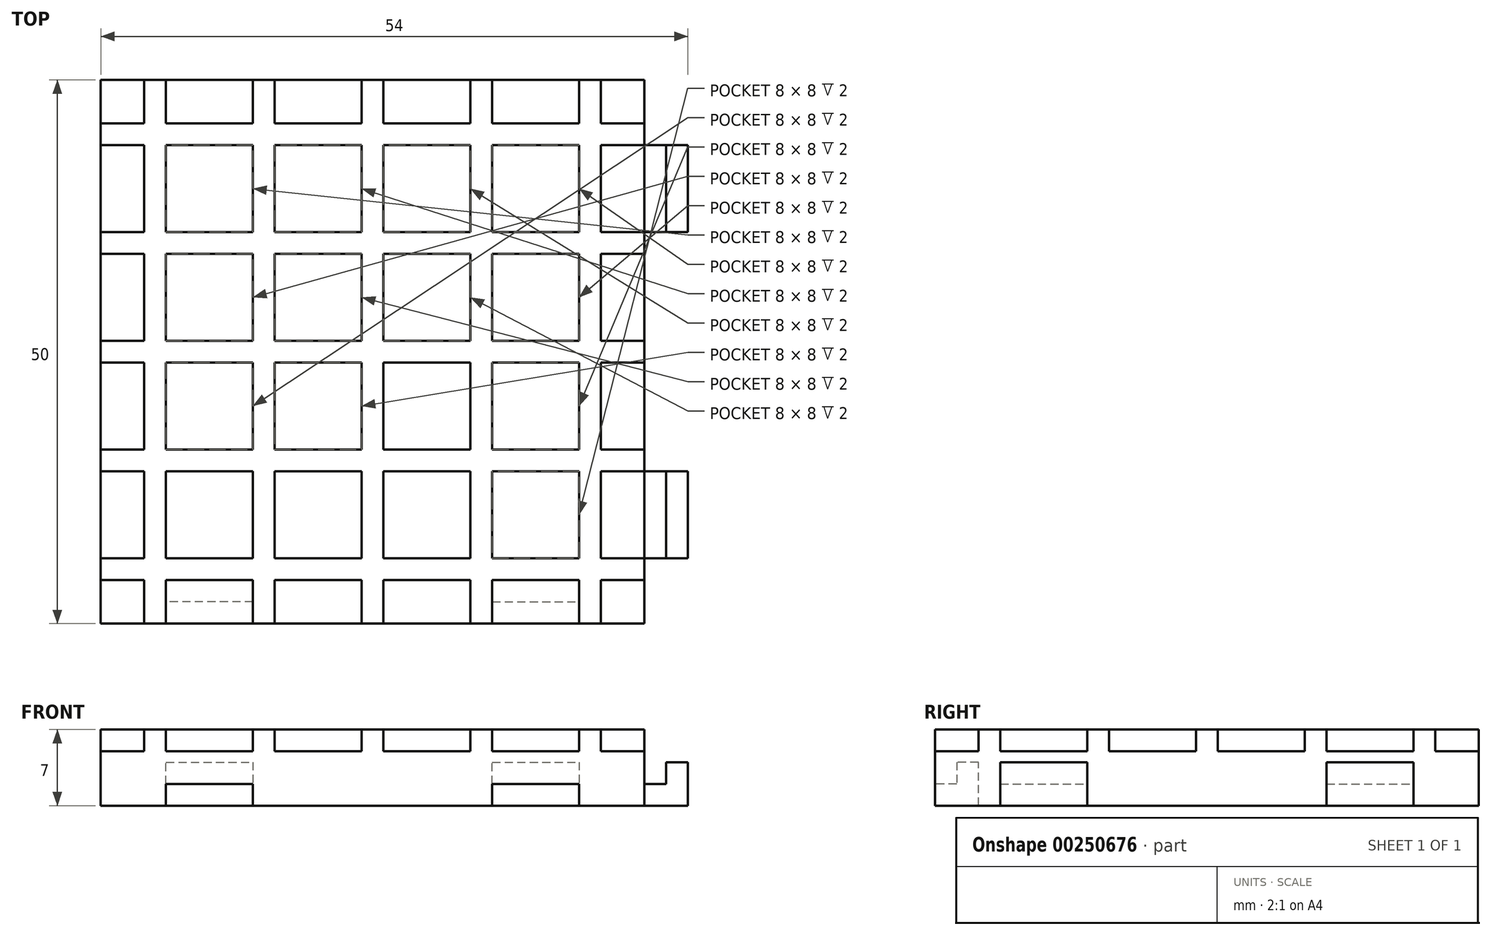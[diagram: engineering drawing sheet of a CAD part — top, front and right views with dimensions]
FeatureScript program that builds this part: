
annotation { "Feature Type Name" : "Feature", "Feature Type Description" : "" }
export const myFeature = defineFeature(function(context is Context, id is Id, definition is map)
    precondition{}
    {
        {
            var Q0;
            Q0=qCreatedBy(makeId("Top.planeOp"),FACE);
            var sketch = newSketch(context, id + "F0", { "sketchPlane" : qUnion([Q0])});
            skLineSegment(sketch, "E0.bottom", {"start": v(-29.37, 40.47) * mm, "end": v(20.63, 40.47) * mm});
            skLineSegment(sketch, "E0.top", {"start": v(-29.37, -9.53) * mm, "end": v(20.63, -9.53) * mm});
            skLineSegment(sketch, "E0.left", {"start": v(-29.37, 40.47) * mm, "end": v(-29.37, -9.53) * mm});
            skLineSegment(sketch, "E0.right", {"start": v(20.63, 40.47) * mm, "end": v(20.63, -9.53) * mm});
            skSolve(sketch);
        }
        {
            var Q0;
            Q0=qSketchRegion(id+"F0",true);
            extrude(context, id + "F1", {"entities" : qUnion([Q0]), "depth" : 5 * mm});
        }
        {
            var Q0;
            Q0=makeQuery(id+"F1.opExtrude","CAP_FACE",FACE,{"disambiguationData":[OSD([sQuery(id+"F0.wireOp",EDGE,"E0.bottom"),sQuery(id+"F0.wireOp",EDGE,"E0.top"),sQuery(id+"F0.wireOp",EDGE,"E0.left"),sQuery(id+"F0.wireOp",EDGE,"E0.right")])],"isStart":false});
            var sketch = newSketch(context, id + "F2", { "sketchPlane" : qUnion([Q0])});
            skLineSegment(sketch, "E1.bottom", {"start": v(-29.37, -5.53) * mm, "end": v(20.63, -5.53) * mm});
            skLineSegment(sketch, "E1.top", {"start": v(-29.37, -3.53) * mm, "end": v(20.63, -3.53) * mm});
            skLineSegment(sketch, "E1.left", {"start": v(-29.37, -5.53) * mm, "end": v(-29.37, -3.53) * mm});
            skLineSegment(sketch, "E1.right", {"start": v(20.63, -5.53) * mm, "end": v(20.63, -3.53) * mm});
            skLineSegment(sketch, "E2.bottom", {"start": v(-29.37, 4.47) * mm, "end": v(20.63, 4.47) * mm});
            skLineSegment(sketch, "E2.top", {"start": v(-29.37, 6.47) * mm, "end": v(20.63, 6.47) * mm});
            skLineSegment(sketch, "E2.left", {"start": v(-29.37, 4.47) * mm, "end": v(-29.37, 6.47) * mm});
            skLineSegment(sketch, "E2.right", {"start": v(20.63, 4.47) * mm, "end": v(20.63, 6.47) * mm});
            skLineSegment(sketch, "E3.bottom", {"start": v(-29.37, 14.47) * mm, "end": v(20.63, 14.47) * mm});
            skLineSegment(sketch, "E3.top", {"start": v(-29.37, 16.47) * mm, "end": v(20.63, 16.47) * mm});
            skLineSegment(sketch, "E3.left", {"start": v(-29.37, 14.47) * mm, "end": v(-29.37, 16.47) * mm});
            skLineSegment(sketch, "E3.right", {"start": v(20.63, 14.47) * mm, "end": v(20.63, 16.47) * mm});
            skLineSegment(sketch, "E4.bottom", {"start": v(-29.37, 24.47) * mm, "end": v(20.63, 24.47) * mm});
            skLineSegment(sketch, "E4.top", {"start": v(-29.37, 26.47) * mm, "end": v(20.63, 26.47) * mm});
            skLineSegment(sketch, "E4.left", {"start": v(-29.37, 24.47) * mm, "end": v(-29.37, 26.47) * mm});
            skLineSegment(sketch, "E4.right", {"start": v(20.63, 24.47) * mm, "end": v(20.63, 26.47) * mm});
            skLineSegment(sketch, "E5.bottom", {"start": v(-29.37, 34.47) * mm, "end": v(20.63, 34.47) * mm});
            skLineSegment(sketch, "E5.top", {"start": v(-29.37, 36.47) * mm, "end": v(20.63, 36.47) * mm});
            skLineSegment(sketch, "E5.left", {"start": v(-29.37, 34.47) * mm, "end": v(-29.37, 36.47) * mm});
            skLineSegment(sketch, "E5.right", {"start": v(20.63, 34.47) * mm, "end": v(20.63, 36.47) * mm});
            skLineSegment(sketch, "E6.bottom", {"start": v(-25.37, -9.53) * mm, "end": v(-23.37, -9.53) * mm});
            skLineSegment(sketch, "E6.top", {"start": v(-25.37, 40.47) * mm, "end": v(-23.37, 40.47) * mm});
            skLineSegment(sketch, "E6.left", {"start": v(-25.37, -9.53) * mm, "end": v(-25.37, 40.47) * mm});
            skLineSegment(sketch, "E6.right", {"start": v(-23.37, -9.53) * mm, "end": v(-23.37, 40.47) * mm});
            skLineSegment(sketch, "E7.bottom", {"start": v(-15.37, -9.53) * mm, "end": v(-13.37, -9.53) * mm});
            skLineSegment(sketch, "E7.top", {"start": v(-15.37, 40.47) * mm, "end": v(-13.37, 40.47) * mm});
            skLineSegment(sketch, "E7.left", {"start": v(-15.37, -9.53) * mm, "end": v(-15.37, 40.47) * mm});
            skLineSegment(sketch, "E7.right", {"start": v(-13.37, -9.53) * mm, "end": v(-13.37, 40.47) * mm});
            skLineSegment(sketch, "E8.bottom", {"start": v(-5.37, -9.53) * mm, "end": v(-3.37, -9.53) * mm});
            skLineSegment(sketch, "E8.top", {"start": v(-5.37, 40.47) * mm, "end": v(-3.37, 40.47) * mm});
            skLineSegment(sketch, "E8.left", {"start": v(-5.37, -9.53) * mm, "end": v(-5.37, 40.47) * mm});
            skLineSegment(sketch, "E8.right", {"start": v(-3.37, -9.53) * mm, "end": v(-3.37, 40.47) * mm});
            skLineSegment(sketch, "E9.bottom", {"start": v(4.63, -9.53) * mm, "end": v(6.63, -9.53) * mm});
            skLineSegment(sketch, "E9.top", {"start": v(4.63, 40.47) * mm, "end": v(6.63, 40.47) * mm});
            skLineSegment(sketch, "E9.left", {"start": v(4.63, -9.53) * mm, "end": v(4.63, 40.47) * mm});
            skLineSegment(sketch, "E9.right", {"start": v(6.63, -9.53) * mm, "end": v(6.63, 40.47) * mm});
            skLineSegment(sketch, "E10.bottom", {"start": v(14.63, -9.53) * mm, "end": v(16.63, -9.53) * mm});
            skLineSegment(sketch, "E10.top", {"start": v(14.63, 40.47) * mm, "end": v(16.63, 40.47) * mm});
            skLineSegment(sketch, "E10.left", {"start": v(14.63, -9.53) * mm, "end": v(14.63, 40.47) * mm});
            skLineSegment(sketch, "E10.right", {"start": v(16.63, -9.53) * mm, "end": v(16.63, 40.47) * mm});
            skSolve(sketch);
        }
        {
            var Q0;
            Q0=makeQuery(id+"F4.boolean.opBoolean","MERGE",FACE,{"derivedFrom":[makeQuery(id+"F1.opExtrude","SWEPT_FACE",FACE,{"disambiguationData":[OSD([sQuery(id+"F0.wireOp",EDGE,"E0.top")])]}),makeQuery(id+"F4.opExtrude","SWEPT_FACE",FACE,{"disambiguationData":[OSD([sQuery(id+"F2.wireOp",EDGE,"E6.bottom")])]}),makeQuery(id+"F4.opExtrude","SWEPT_FACE",FACE,{"disambiguationData":[OSD([sQuery(id+"F2.wireOp",EDGE,"E7.bottom")])]}),makeQuery(id+"F4.opExtrude","SWEPT_FACE",FACE,{"disambiguationData":[OSD([sQuery(id+"F2.wireOp",EDGE,"E8.bottom")])]}),makeQuery(id+"F4.opExtrude","SWEPT_FACE",FACE,{"disambiguationData":[OSD([sQuery(id+"F2.wireOp",EDGE,"E9.bottom")])]}),makeQuery(id+"F4.opExtrude","SWEPT_FACE",FACE,{"disambiguationData":[OSD([sQuery(id+"F2.wireOp",EDGE,"E10.bottom")])]})]});
            var sketch = newSketch(context, id + "F3", { "sketchPlane" : qUnion([Q0])});
            skLineSegment(sketch, "E11.bottom", {"start": v(-23.37, 0) * mm, "end": v(-15.37, 0) * mm});
            skLineSegment(sketch, "E11.top", {"start": v(-23.37, 2) * mm, "end": v(-15.37, 2) * mm});
            skLineSegment(sketch, "E11.left", {"start": v(-23.37, 0) * mm, "end": v(-23.37, 2) * mm});
            skLineSegment(sketch, "E11.right", {"start": v(-15.37, 0) * mm, "end": v(-15.37, 2) * mm});
            skLineSegment(sketch, "E12.bottom", {"start": v(6.63, 0) * mm, "end": v(14.63, 0) * mm});
            skLineSegment(sketch, "E12.top", {"start": v(6.63, 2) * mm, "end": v(14.63, 2) * mm});
            skLineSegment(sketch, "E12.left", {"start": v(6.63, 0) * mm, "end": v(6.63, 2) * mm});
            skLineSegment(sketch, "E12.right", {"start": v(14.63, 0) * mm, "end": v(14.63, 2) * mm});
            skSolve(sketch);
        }
        {
            var Q0;
            Q0=qSketchRegion(id+"F2",true);
            var Q1;
            {var subQ0=sQuery(id+"F2.wireOp",EDGE,"E7.left");var subQ1=sQuery(id+"F2.wireOp",EDGE,"E1.top");var subQ2=makeQuery(id+"F2.imprint","INTERSECT",VERTEX,{"derivedFrom":[subQ1,subQ0]});Q1=makeQuery(id+"F2.imprint","IMPRINT",FACE,{"disambiguationData":[TD([[makeQuery(id+"F2.imprint","IMPRINT",EDGE,{"disambiguationData":[TD([[subQ2,-1.0]])],"derivedFrom":subQ1}),1.0]])]});}
            var Q2;
            {var subQ0=sQuery(id+"F2.wireOp",EDGE,"E7.left");var subQ1=sQuery(id+"F2.wireOp",EDGE,"E2.bottom");var subQ2=makeQuery(id+"F2.imprint","INTERSECT",VERTEX,{"derivedFrom":[subQ1,subQ0]});Q2=makeQuery(id+"F2.imprint","IMPRINT",FACE,{"disambiguationData":[TD([[makeQuery(id+"F2.imprint","IMPRINT",EDGE,{"disambiguationData":[TD([[subQ2,-1.0]])],"derivedFrom":subQ1}),1.0]])]});}
            var Q3;
            {var subQ0=sQuery(id+"F2.wireOp",EDGE,"E7.right");var subQ1=sQuery(id+"F2.wireOp",EDGE,"E2.bottom");var subQ2=makeQuery(id+"F2.imprint","INTERSECT",VERTEX,{"derivedFrom":[subQ1,subQ0]});Q3=makeQuery(id+"F2.imprint","IMPRINT",FACE,{"disambiguationData":[TD([[makeQuery(id+"F2.imprint","IMPRINT",EDGE,{"disambiguationData":[TD([[subQ2,-1.0]])],"derivedFrom":subQ1}),1.0]])]});}
            var Q4;
            {var subQ0=sQuery(id+"F2.wireOp",EDGE,"E7.left");var subQ1=sQuery(id+"F2.wireOp",EDGE,"E2.top");var subQ2=makeQuery(id+"F2.imprint","INTERSECT",VERTEX,{"derivedFrom":[subQ1,subQ0]});Q4=makeQuery(id+"F2.imprint","IMPRINT",FACE,{"disambiguationData":[TD([[makeQuery(id+"F2.imprint","IMPRINT",EDGE,{"disambiguationData":[TD([[subQ2,-1.0]])],"derivedFrom":subQ1}),1.0]])]});}
            var Q5;
            {var subQ0=sQuery(id+"F2.wireOp",EDGE,"E7.left");var subQ1=sQuery(id+"F2.wireOp",EDGE,"E3.bottom");var subQ2=makeQuery(id+"F2.imprint","INTERSECT",VERTEX,{"derivedFrom":[subQ1,subQ0]});Q5=makeQuery(id+"F2.imprint","IMPRINT",FACE,{"disambiguationData":[TD([[makeQuery(id+"F2.imprint","IMPRINT",EDGE,{"disambiguationData":[TD([[subQ2,-1.0]])],"derivedFrom":subQ1}),1.0]])]});}
            var Q6;
            {var subQ0=sQuery(id+"F2.wireOp",EDGE,"E6.right");var subQ1=sQuery(id+"F2.wireOp",EDGE,"E3.bottom");var subQ2=makeQuery(id+"F2.imprint","INTERSECT",VERTEX,{"derivedFrom":[subQ1,subQ0]});Q6=makeQuery(id+"F2.imprint","IMPRINT",FACE,{"disambiguationData":[TD([[makeQuery(id+"F2.imprint","IMPRINT",EDGE,{"disambiguationData":[TD([[subQ2,-1.0]])],"derivedFrom":subQ1}),1.0]])]});}
            var Q7;
            {var subQ0=sQuery(id+"F2.wireOp",EDGE,"E6.right");var subQ1=sQuery(id+"F2.wireOp",EDGE,"E4.bottom");var subQ2=makeQuery(id+"F2.imprint","INTERSECT",VERTEX,{"derivedFrom":[subQ1,subQ0]});Q7=makeQuery(id+"F2.imprint","IMPRINT",FACE,{"disambiguationData":[TD([[makeQuery(id+"F2.imprint","IMPRINT",EDGE,{"disambiguationData":[TD([[subQ2,-1.0]])],"derivedFrom":subQ1}),1.0]])]});}
            var Q8;
            {var subQ0=sQuery(id+"F2.wireOp",EDGE,"E7.left");var subQ1=sQuery(id+"F2.wireOp",EDGE,"E4.bottom");var subQ2=makeQuery(id+"F2.imprint","INTERSECT",VERTEX,{"derivedFrom":[subQ1,subQ0]});Q8=makeQuery(id+"F2.imprint","IMPRINT",FACE,{"disambiguationData":[TD([[makeQuery(id+"F2.imprint","IMPRINT",EDGE,{"disambiguationData":[TD([[subQ2,-1.0]])],"derivedFrom":subQ1}),1.0]])]});}
            var Q9;
            {var subQ0=sQuery(id+"F2.wireOp",EDGE,"E7.left");var subQ1=sQuery(id+"F2.wireOp",EDGE,"E4.top");var subQ2=makeQuery(id+"F2.imprint","INTERSECT",VERTEX,{"derivedFrom":[subQ1,subQ0]});Q9=makeQuery(id+"F2.imprint","IMPRINT",FACE,{"disambiguationData":[TD([[makeQuery(id+"F2.imprint","IMPRINT",EDGE,{"disambiguationData":[TD([[subQ2,-1.0]])],"derivedFrom":subQ1}),1.0]])]});}
            var Q10;
            {var subQ0=sQuery(id+"F2.wireOp",EDGE,"E7.left");var subQ1=sQuery(id+"F2.wireOp",EDGE,"E3.top");var subQ2=makeQuery(id+"F2.imprint","INTERSECT",VERTEX,{"derivedFrom":[subQ1,subQ0]});Q10=makeQuery(id+"F2.imprint","IMPRINT",FACE,{"disambiguationData":[TD([[makeQuery(id+"F2.imprint","IMPRINT",EDGE,{"disambiguationData":[TD([[subQ2,-1.0]])],"derivedFrom":subQ1}),1.0]])]});}
            var Q11;
            {var subQ0=sQuery(id+"F2.wireOp",EDGE,"E7.right");var subQ1=sQuery(id+"F2.wireOp",EDGE,"E4.bottom");var subQ2=makeQuery(id+"F2.imprint","INTERSECT",VERTEX,{"derivedFrom":[subQ1,subQ0]});Q11=makeQuery(id+"F2.imprint","IMPRINT",FACE,{"disambiguationData":[TD([[makeQuery(id+"F2.imprint","IMPRINT",EDGE,{"disambiguationData":[TD([[subQ2,-1.0]])],"derivedFrom":subQ1}),1.0]])]});}
            var Q12;
            {var subQ0=sQuery(id+"F2.wireOp",EDGE,"E8.left");var subQ1=sQuery(id+"F2.wireOp",EDGE,"E3.top");var subQ2=makeQuery(id+"F2.imprint","INTERSECT",VERTEX,{"derivedFrom":[subQ1,subQ0]});Q12=makeQuery(id+"F2.imprint","IMPRINT",FACE,{"disambiguationData":[TD([[makeQuery(id+"F2.imprint","IMPRINT",EDGE,{"disambiguationData":[TD([[subQ2,-1.0]])],"derivedFrom":subQ1}),1.0]])]});}
            var Q13;
            {var subQ0=sQuery(id+"F2.wireOp",EDGE,"E8.left");var subQ1=sQuery(id+"F2.wireOp",EDGE,"E3.bottom");var subQ2=makeQuery(id+"F2.imprint","INTERSECT",VERTEX,{"derivedFrom":[subQ1,subQ0]});Q13=makeQuery(id+"F2.imprint","IMPRINT",FACE,{"disambiguationData":[TD([[makeQuery(id+"F2.imprint","IMPRINT",EDGE,{"disambiguationData":[TD([[subQ2,-1.0]])],"derivedFrom":subQ1}),1.0]])]});}
            var Q14;
            {var subQ0=sQuery(id+"F2.wireOp",EDGE,"E7.right");var subQ1=sQuery(id+"F2.wireOp",EDGE,"E3.bottom");var subQ2=makeQuery(id+"F2.imprint","INTERSECT",VERTEX,{"derivedFrom":[subQ1,subQ0]});Q14=makeQuery(id+"F2.imprint","IMPRINT",FACE,{"disambiguationData":[TD([[makeQuery(id+"F2.imprint","IMPRINT",EDGE,{"disambiguationData":[TD([[subQ2,-1.0]])],"derivedFrom":subQ1}),1.0]])]});}
            var Q15;
            {var subQ0=sQuery(id+"F2.wireOp",EDGE,"E8.left");var subQ1=sQuery(id+"F2.wireOp",EDGE,"E2.top");var subQ2=makeQuery(id+"F2.imprint","INTERSECT",VERTEX,{"derivedFrom":[subQ1,subQ0]});Q15=makeQuery(id+"F2.imprint","IMPRINT",FACE,{"disambiguationData":[TD([[makeQuery(id+"F2.imprint","IMPRINT",EDGE,{"disambiguationData":[TD([[subQ2,-1.0]])],"derivedFrom":subQ1}),1.0]])]});}
            var Q16;
            {var subQ0=sQuery(id+"F2.wireOp",EDGE,"E8.left");var subQ1=sQuery(id+"F2.wireOp",EDGE,"E2.bottom");var subQ2=makeQuery(id+"F2.imprint","INTERSECT",VERTEX,{"derivedFrom":[subQ1,subQ0]});Q16=makeQuery(id+"F2.imprint","IMPRINT",FACE,{"disambiguationData":[TD([[makeQuery(id+"F2.imprint","IMPRINT",EDGE,{"disambiguationData":[TD([[subQ2,-1.0]])],"derivedFrom":subQ1}),1.0]])]});}
            var Q17;
            {var subQ0=sQuery(id+"F2.wireOp",EDGE,"E8.left");var subQ1=sQuery(id+"F2.wireOp",EDGE,"E1.top");var subQ2=makeQuery(id+"F2.imprint","INTERSECT",VERTEX,{"derivedFrom":[subQ1,subQ0]});Q17=makeQuery(id+"F2.imprint","IMPRINT",FACE,{"disambiguationData":[TD([[makeQuery(id+"F2.imprint","IMPRINT",EDGE,{"disambiguationData":[TD([[subQ2,-1.0]])],"derivedFrom":subQ1}),1.0]])]});}
            var Q18;
            {var subQ0=sQuery(id+"F2.wireOp",EDGE,"E8.right");var subQ1=sQuery(id+"F2.wireOp",EDGE,"E2.bottom");var subQ2=makeQuery(id+"F2.imprint","INTERSECT",VERTEX,{"derivedFrom":[subQ1,subQ0]});Q18=makeQuery(id+"F2.imprint","IMPRINT",FACE,{"disambiguationData":[TD([[makeQuery(id+"F2.imprint","IMPRINT",EDGE,{"disambiguationData":[TD([[subQ2,-1.0]])],"derivedFrom":subQ1}),1.0]])]});}
            var Q19;
            {var subQ0=sQuery(id+"F2.wireOp",EDGE,"E9.left");var subQ1=sQuery(id+"F2.wireOp",EDGE,"E1.top");var subQ2=makeQuery(id+"F2.imprint","INTERSECT",VERTEX,{"derivedFrom":[subQ1,subQ0]});Q19=makeQuery(id+"F2.imprint","IMPRINT",FACE,{"disambiguationData":[TD([[makeQuery(id+"F2.imprint","IMPRINT",EDGE,{"disambiguationData":[TD([[subQ2,-1.0]])],"derivedFrom":subQ1}),1.0]])]});}
            var Q20;
            {var subQ0=sQuery(id+"F2.wireOp",EDGE,"E9.left");var subQ1=sQuery(id+"F2.wireOp",EDGE,"E2.bottom");var subQ2=makeQuery(id+"F2.imprint","INTERSECT",VERTEX,{"derivedFrom":[subQ1,subQ0]});Q20=makeQuery(id+"F2.imprint","IMPRINT",FACE,{"disambiguationData":[TD([[makeQuery(id+"F2.imprint","IMPRINT",EDGE,{"disambiguationData":[TD([[subQ2,-1.0]])],"derivedFrom":subQ1}),1.0]])]});}
            var Q21;
            {var subQ0=sQuery(id+"F2.wireOp",EDGE,"E9.right");var subQ1=sQuery(id+"F2.wireOp",EDGE,"E2.bottom");var subQ2=makeQuery(id+"F2.imprint","INTERSECT",VERTEX,{"derivedFrom":[subQ1,subQ0]});Q21=makeQuery(id+"F2.imprint","IMPRINT",FACE,{"disambiguationData":[TD([[makeQuery(id+"F2.imprint","IMPRINT",EDGE,{"disambiguationData":[TD([[subQ2,-1.0]])],"derivedFrom":subQ1}),1.0]])]});}
            var Q22;
            {var subQ0=sQuery(id+"F2.wireOp",EDGE,"E9.left");var subQ1=sQuery(id+"F2.wireOp",EDGE,"E2.top");var subQ2=makeQuery(id+"F2.imprint","INTERSECT",VERTEX,{"derivedFrom":[subQ1,subQ0]});Q22=makeQuery(id+"F2.imprint","IMPRINT",FACE,{"disambiguationData":[TD([[makeQuery(id+"F2.imprint","IMPRINT",EDGE,{"disambiguationData":[TD([[subQ2,-1.0]])],"derivedFrom":subQ1}),1.0]])]});}
            var Q23;
            {var subQ0=sQuery(id+"F2.wireOp",EDGE,"E9.right");var subQ1=sQuery(id+"F2.wireOp",EDGE,"E3.bottom");var subQ2=makeQuery(id+"F2.imprint","INTERSECT",VERTEX,{"derivedFrom":[subQ1,subQ0]});Q23=makeQuery(id+"F2.imprint","IMPRINT",FACE,{"disambiguationData":[TD([[makeQuery(id+"F2.imprint","IMPRINT",EDGE,{"disambiguationData":[TD([[subQ2,-1.0]])],"derivedFrom":subQ1}),1.0]])]});}
            var Q24;
            {var subQ0=sQuery(id+"F2.wireOp",EDGE,"E9.left");var subQ1=sQuery(id+"F2.wireOp",EDGE,"E3.bottom");var subQ2=makeQuery(id+"F2.imprint","INTERSECT",VERTEX,{"derivedFrom":[subQ1,subQ0]});Q24=makeQuery(id+"F2.imprint","IMPRINT",FACE,{"disambiguationData":[TD([[makeQuery(id+"F2.imprint","IMPRINT",EDGE,{"disambiguationData":[TD([[subQ2,-1.0]])],"derivedFrom":subQ1}),1.0]])]});}
            var Q25;
            {var subQ0=sQuery(id+"F2.wireOp",EDGE,"E8.right");var subQ1=sQuery(id+"F2.wireOp",EDGE,"E3.bottom");var subQ2=makeQuery(id+"F2.imprint","INTERSECT",VERTEX,{"derivedFrom":[subQ1,subQ0]});Q25=makeQuery(id+"F2.imprint","IMPRINT",FACE,{"disambiguationData":[TD([[makeQuery(id+"F2.imprint","IMPRINT",EDGE,{"disambiguationData":[TD([[subQ2,-1.0]])],"derivedFrom":subQ1}),1.0]])]});}
            var Q26;
            {var subQ0=sQuery(id+"F2.wireOp",EDGE,"E9.left");var subQ1=sQuery(id+"F2.wireOp",EDGE,"E3.top");var subQ2=makeQuery(id+"F2.imprint","INTERSECT",VERTEX,{"derivedFrom":[subQ1,subQ0]});Q26=makeQuery(id+"F2.imprint","IMPRINT",FACE,{"disambiguationData":[TD([[makeQuery(id+"F2.imprint","IMPRINT",EDGE,{"disambiguationData":[TD([[subQ2,-1.0]])],"derivedFrom":subQ1}),1.0]])]});}
            var Q27;
            {var subQ0=sQuery(id+"F2.wireOp",EDGE,"E9.left");var subQ1=sQuery(id+"F2.wireOp",EDGE,"E4.bottom");var subQ2=makeQuery(id+"F2.imprint","INTERSECT",VERTEX,{"derivedFrom":[subQ1,subQ0]});Q27=makeQuery(id+"F2.imprint","IMPRINT",FACE,{"disambiguationData":[TD([[makeQuery(id+"F2.imprint","IMPRINT",EDGE,{"disambiguationData":[TD([[subQ2,-1.0]])],"derivedFrom":subQ1}),1.0]])]});}
            var Q28;
            {var subQ0=sQuery(id+"F2.wireOp",EDGE,"E8.right");var subQ1=sQuery(id+"F2.wireOp",EDGE,"E4.bottom");var subQ2=makeQuery(id+"F2.imprint","INTERSECT",VERTEX,{"derivedFrom":[subQ1,subQ0]});Q28=makeQuery(id+"F2.imprint","IMPRINT",FACE,{"disambiguationData":[TD([[makeQuery(id+"F2.imprint","IMPRINT",EDGE,{"disambiguationData":[TD([[subQ2,-1.0]])],"derivedFrom":subQ1}),1.0]])]});}
            var Q29;
            {var subQ0=sQuery(id+"F2.wireOp",EDGE,"E8.left");var subQ1=sQuery(id+"F2.wireOp",EDGE,"E4.top");var subQ2=makeQuery(id+"F2.imprint","INTERSECT",VERTEX,{"derivedFrom":[subQ1,subQ0]});Q29=makeQuery(id+"F2.imprint","IMPRINT",FACE,{"disambiguationData":[TD([[makeQuery(id+"F2.imprint","IMPRINT",EDGE,{"disambiguationData":[TD([[subQ2,-1.0]])],"derivedFrom":subQ1}),1.0]])]});}
            var Q30;
            {var subQ0=sQuery(id+"F2.wireOp",EDGE,"E8.left");var subQ1=sQuery(id+"F2.wireOp",EDGE,"E4.bottom");var subQ2=makeQuery(id+"F2.imprint","INTERSECT",VERTEX,{"derivedFrom":[subQ1,subQ0]});Q30=makeQuery(id+"F2.imprint","IMPRINT",FACE,{"disambiguationData":[TD([[makeQuery(id+"F2.imprint","IMPRINT",EDGE,{"disambiguationData":[TD([[subQ2,-1.0]])],"derivedFrom":subQ1}),1.0]])]});}
            var Q31;
            {var subQ0=sQuery(id+"F2.wireOp",EDGE,"E9.left");var subQ1=sQuery(id+"F2.wireOp",EDGE,"E4.top");var subQ2=makeQuery(id+"F2.imprint","INTERSECT",VERTEX,{"derivedFrom":[subQ1,subQ0]});Q31=makeQuery(id+"F2.imprint","IMPRINT",FACE,{"disambiguationData":[TD([[makeQuery(id+"F2.imprint","IMPRINT",EDGE,{"disambiguationData":[TD([[subQ2,-1.0]])],"derivedFrom":subQ1}),1.0]])]});}
            var Q32;
            {var subQ0=sQuery(id+"F2.wireOp",EDGE,"E9.right");var subQ1=sQuery(id+"F2.wireOp",EDGE,"E4.bottom");var subQ2=makeQuery(id+"F2.imprint","INTERSECT",VERTEX,{"derivedFrom":[subQ1,subQ0]});Q32=makeQuery(id+"F2.imprint","IMPRINT",FACE,{"disambiguationData":[TD([[makeQuery(id+"F2.imprint","IMPRINT",EDGE,{"disambiguationData":[TD([[subQ2,-1.0]])],"derivedFrom":subQ1}),1.0]])]});}
            var Q33;
            {var subQ0=sQuery(id+"F2.wireOp",EDGE,"E6.right");var subQ1=sQuery(id+"F2.wireOp",EDGE,"E2.bottom");var subQ2=makeQuery(id+"F2.imprint","INTERSECT",VERTEX,{"derivedFrom":[subQ1,subQ0]});Q33=makeQuery(id+"F2.imprint","IMPRINT",FACE,{"disambiguationData":[TD([[makeQuery(id+"F2.imprint","IMPRINT",EDGE,{"disambiguationData":[TD([[subQ2,-1.0]])],"derivedFrom":subQ1}),1.0]])]});}
            extrude(context, id + "F4", {"entities" : qUnion([Q0, Q1, Q2, Q3, Q4, Q5, Q6, Q7, Q8, Q9, Q10, Q11, Q12, Q13, Q14, Q15, Q16, Q17, Q18, Q19, Q20, Q21, Q22, Q23, Q24, Q25, Q26, Q27, Q28, Q29, Q30, Q31, Q32, Q33]), "operationType" : NewBodyOperationType.ADD, "depth" : 2 * mm});
        }
        {
            var Q0;
            Q0=qSketchRegion(id+"F3",true);
            extrude(context, id + "F5", {"entities" : qUnion([Q0]), "operationType" : NewBodyOperationType.REMOVE, "oppositeDirection" : true, "depth" : 4 * mm});
        }
        {
            var Q0;
            Q0=makeQuery(id+"F4.boolean.opBoolean","MERGE",FACE,{"derivedFrom":[makeQuery(id+"F1.opExtrude","SWEPT_FACE",FACE,{"disambiguationData":[OSD([sQuery(id+"F0.wireOp",EDGE,"E0.right")])]}),makeQuery(id+"F4.opExtrude","SWEPT_FACE",FACE,{"disambiguationData":[OSD([sQuery(id+"F2.wireOp",EDGE,"E1.right")])]}),makeQuery(id+"F4.opExtrude","SWEPT_FACE",FACE,{"disambiguationData":[OSD([sQuery(id+"F2.wireOp",EDGE,"E2.right")])]}),makeQuery(id+"F4.opExtrude","SWEPT_FACE",FACE,{"disambiguationData":[OSD([sQuery(id+"F2.wireOp",EDGE,"E3.right")])]}),makeQuery(id+"F4.opExtrude","SWEPT_FACE",FACE,{"disambiguationData":[OSD([sQuery(id+"F2.wireOp",EDGE,"E4.right")])]}),makeQuery(id+"F4.opExtrude","SWEPT_FACE",FACE,{"disambiguationData":[OSD([sQuery(id+"F2.wireOp",EDGE,"E5.right")])]})]});
            var sketch = newSketch(context, id + "F6", { "sketchPlane" : qUnion([Q0])});
            skLineSegment(sketch, "E13.bottom", {"start": v(-3.53, 0) * mm, "end": v(4.47, 0) * mm});
            skLineSegment(sketch, "E13.top", {"start": v(-3.53, 2) * mm, "end": v(4.47, 2) * mm});
            skLineSegment(sketch, "E13.left", {"start": v(-3.53, 0) * mm, "end": v(-3.53, 2) * mm});
            skLineSegment(sketch, "E13.right", {"start": v(4.47, 0) * mm, "end": v(4.47, 2) * mm});
            skLineSegment(sketch, "E14.bottom", {"start": v(26.47, 0) * mm, "end": v(34.47, 0) * mm});
            skLineSegment(sketch, "E14.top", {"start": v(26.47, 2) * mm, "end": v(34.47, 2) * mm});
            skLineSegment(sketch, "E14.left", {"start": v(26.47, 0) * mm, "end": v(26.47, 2) * mm});
            skLineSegment(sketch, "E14.right", {"start": v(34.47, 0) * mm, "end": v(34.47, 2) * mm});
            skSolve(sketch);
        }
        {
            var Q0;
            Q0=qSketchRegion(id+"F6",true);
            extrude(context, id + "F7", {"entities" : qUnion([Q0]), "operationType" : NewBodyOperationType.ADD, "depth" : 4 * mm});
        }
        {
            var Q0;
            Q0=makeQuery(id+"F7.opExtrude","SWEPT_FACE",FACE,{"disambiguationData":[OSD([sQuery(id+"F6.wireOp",EDGE,"E14.top")])]});
            var sketch = newSketch(context, id + "F8", { "sketchPlane" : qUnion([Q0])});
            skLineSegment(sketch, "E15.bottom", {"start": v(24.63, 34.47) * mm, "end": v(22.63, 34.47) * mm});
            skLineSegment(sketch, "E15.top", {"start": v(24.63, 26.47) * mm, "end": v(22.63, 26.47) * mm});
            skLineSegment(sketch, "E15.left", {"start": v(24.63, 34.47) * mm, "end": v(24.63, 26.47) * mm});
            skLineSegment(sketch, "E15.right", {"start": v(22.63, 34.47) * mm, "end": v(22.63, 26.47) * mm});
            skSolve(sketch);
        }
        {
            var Q0;
            Q0=qSketchRegion(id+"F8",true);
            extrude(context, id + "F9", {"entities" : qUnion([Q0]), "operationType" : NewBodyOperationType.ADD, "depth" : 2 * mm});
        }
        {
            var Q0;
            Q0=makeQuery(id+"F7.opExtrude","SWEPT_FACE",FACE,{"disambiguationData":[OSD([sQuery(id+"F6.wireOp",EDGE,"E13.top")])]});
            var sketch = newSketch(context, id + "F10", { "sketchPlane" : qUnion([Q0])});
            skLineSegment(sketch, "E16.bottom", {"start": v(24.63, 4.47) * mm, "end": v(22.63, 4.47) * mm});
            skLineSegment(sketch, "E16.top", {"start": v(24.63, -3.53) * mm, "end": v(22.63, -3.53) * mm});
            skLineSegment(sketch, "E16.left", {"start": v(24.63, 4.47) * mm, "end": v(24.63, -3.53) * mm});
            skLineSegment(sketch, "E16.right", {"start": v(22.63, 4.47) * mm, "end": v(22.63, -3.53) * mm});
            skSolve(sketch);
        }
        {
            var Q0;
            Q0=qSketchRegion(id+"F10",true);
            extrude(context, id + "F11", {"entities" : qUnion([Q0]), "operationType" : NewBodyOperationType.ADD, "depth" : 2 * mm});
        }
        {
            var Q0;
            Q0=makeQuery(id+"F5.boolean.opBoolean","COPY",FACE,{"derivedFrom":makeQuery(id+"F5.opExtrude","SWEPT_FACE",FACE,{"disambiguationData":[OSD([sQuery(id+"F3.wireOp",EDGE,"E12.top")])]})});
            var sketch = newSketch(context, id + "F12", { "sketchPlane" : qUnion([Q0])});
            skLineSegment(sketch, "E17.bottom", {"start": v(6.63, 5.53) * mm, "end": v(14.63, 5.53) * mm});
            skLineSegment(sketch, "E17.top", {"start": v(6.63, 7.53) * mm, "end": v(14.63, 7.53) * mm});
            skLineSegment(sketch, "E17.left", {"start": v(6.63, 5.53) * mm, "end": v(6.63, 7.53) * mm});
            skLineSegment(sketch, "E17.right", {"start": v(14.63, 5.53) * mm, "end": v(14.63, 7.53) * mm});
            skSolve(sketch);
        }
        {
            var Q0;
            Q0=qSketchRegion(id+"F12",true);
            extrude(context, id + "F13", {"entities" : qUnion([Q0]), "operationType" : NewBodyOperationType.REMOVE, "oppositeDirection" : true, "depth" : 2 * mm});
        }
        {
            var Q0;
            Q0=makeQuery(id+"F5.boolean.opBoolean","COPY",FACE,{"derivedFrom":makeQuery(id+"F5.opExtrude","SWEPT_FACE",FACE,{"disambiguationData":[OSD([sQuery(id+"F3.wireOp",EDGE,"E11.top")])]})});
            var sketch = newSketch(context, id + "F14", { "sketchPlane" : qUnion([Q0])});
            skLineSegment(sketch, "E18.bottom", {"start": v(-15.37, 5.53) * mm, "end": v(-23.37, 5.53) * mm});
            skLineSegment(sketch, "E18.top", {"start": v(-15.37, 7.53) * mm, "end": v(-23.37, 7.53) * mm});
            skLineSegment(sketch, "E18.left", {"start": v(-15.37, 5.53) * mm, "end": v(-15.37, 7.53) * mm});
            skLineSegment(sketch, "E18.right", {"start": v(-23.37, 5.53) * mm, "end": v(-23.37, 7.53) * mm});
            skSolve(sketch);
        }
        {
            var Q0;
            Q0=qSketchRegion(id+"F14",true);
            extrude(context, id + "F15", {"entities" : qUnion([Q0]), "operationType" : NewBodyOperationType.REMOVE, "oppositeDirection" : true, "depth" : 2 * mm});
        }
    });
